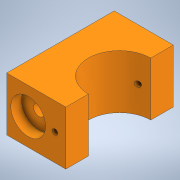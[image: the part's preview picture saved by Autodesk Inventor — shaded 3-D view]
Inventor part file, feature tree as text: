
AUTODESK INVENTOR PART (.ipt)
format: ipt  version: 2022 (Build 260153000, 153)  size: 130,560 bytes
history: native  units: mm
features: sketch x3, hole x2, extrude x1
ambient origin geometry x8: Origin, YZ Plane, XZ Plane, XY Plane, X Axis, Y Axis, Z Axis, Center Point
bodies: Solid1 (feature_tree)
feature tree (6):
  extrude  "Extrusion1"  Depth=55.0mm
  hole  "Hole1"  [1 undecoded]
  hole  "Hole2"  [1 undecoded]
  sketch  "Sketch1"  dims[d0=100.0mm d1=55.0mm]
  sketch  "Sketch2"  dims[d3=58.0mm d4=50.0mm d5=0.0mm]
  sketch  "Sketch4"  dims[d7=10.0mm d8=6.0mm d9=32.4mm d10=10.0mm d11=90.0deg d12=8.0mm d13=0.0mm d14=20.0mm d15=10.0mm d16=5.0mm d17=6.0mm d18=4.0mm d19=2.0mm d20=90.0deg d21=8.0mm d22=20.594885mm]
note: 2 required parameter values undecoded (feature->parameter linkage not recoverable at this tier; creation-order binding heuristic only, values carry confidence <= 0.55)
